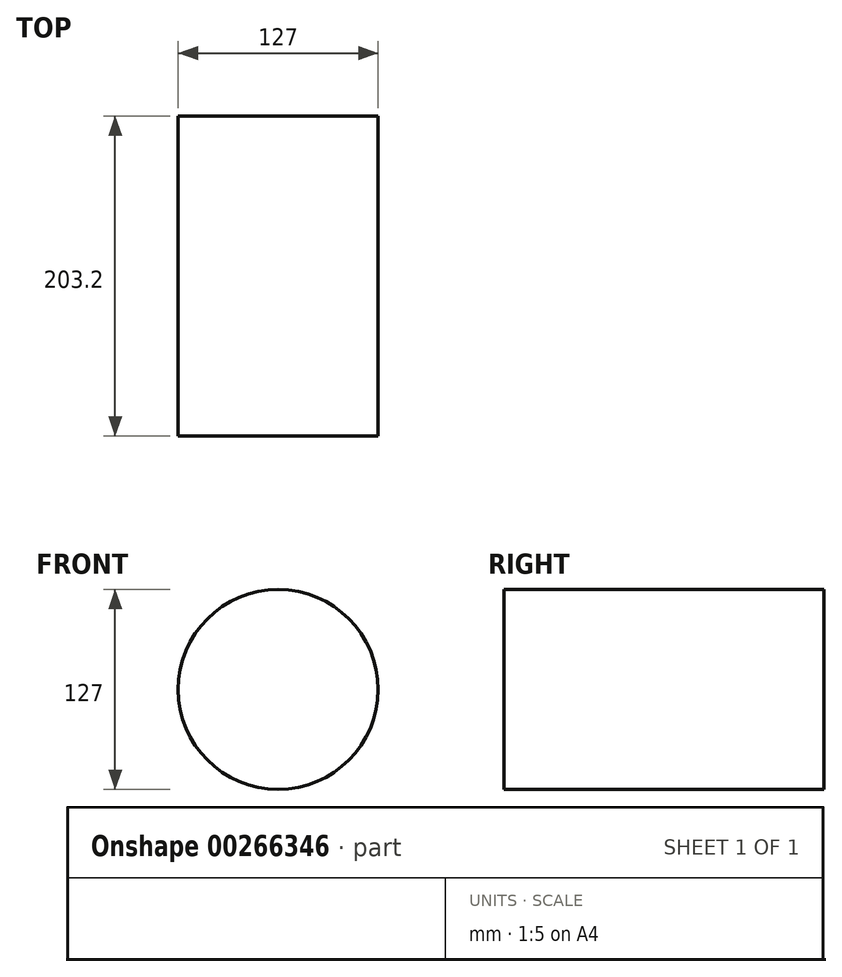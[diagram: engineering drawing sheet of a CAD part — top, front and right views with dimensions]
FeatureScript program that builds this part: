
annotation { "Feature Type Name" : "Feature", "Feature Type Description" : "" }
export const myFeature = defineFeature(function(context is Context, id is Id, definition is map)
    precondition{}
    {
        {
            var Q0;
            Q0=qCreatedBy(makeId("Front.planeOp"),FACE);
            var sketch = newSketch(context, id + "F0", { "sketchPlane" : qUnion([Q0])});
            skCircle(sketch, "E0", {"center": v(0, 0) * mm, "radius": 63.5 * mm});
            skSolve(sketch);
        }
        {
            var Q0;
            Q0=makeQuery(id+"F0.imprint","IMPRINT",FACE,{"disambiguationData":[TD([[makeQuery(id+"F0.imprint","IMPRINT",EDGE,{"derivedFrom":sQuery(id+"F0.wireOp",EDGE,"E0")}),1.0]])]});
            extrude(context, id + "F1", {"entities" : qUnion([Q0]), "depth" : 203.2 * mm});
        }
    });
